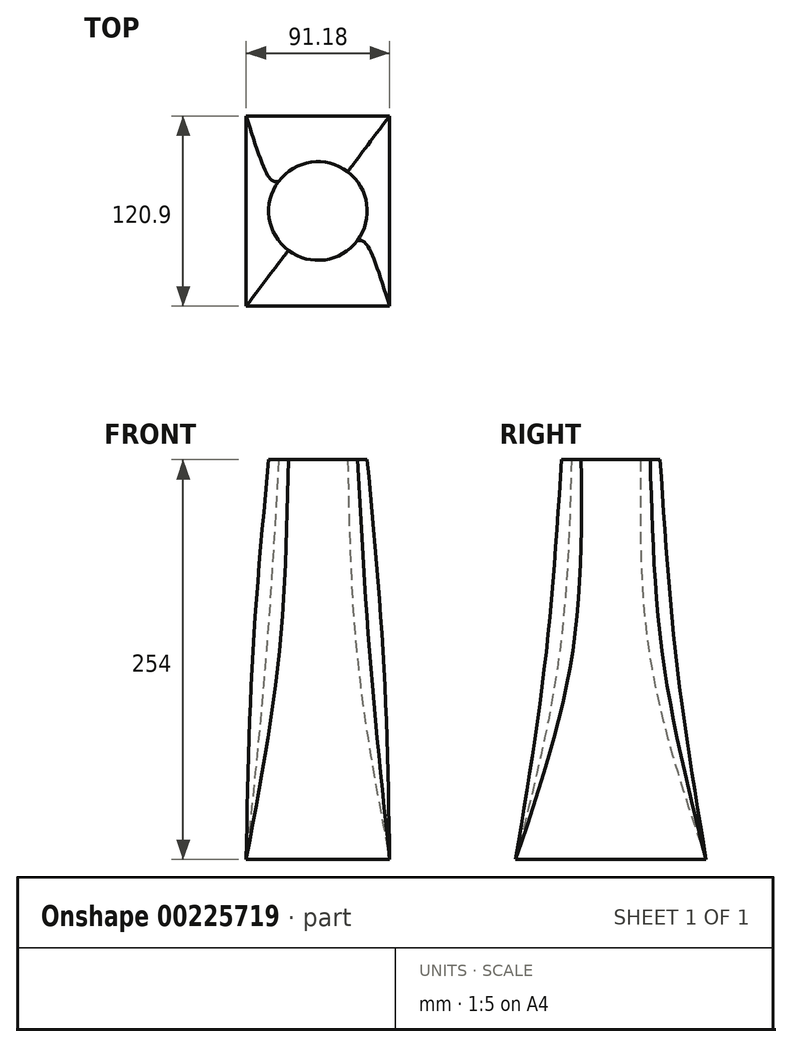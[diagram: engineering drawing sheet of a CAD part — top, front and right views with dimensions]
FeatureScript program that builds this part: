
annotation { "Feature Type Name" : "Feature", "Feature Type Description" : "" }
export const myFeature = defineFeature(function(context is Context, id is Id, definition is map)
    precondition{}
    {
        {
            var Q0;
            Q0=qCreatedBy(makeId("Top.planeOp"),FACE);
            var sketch = newSketch(context, id + "F0", { "sketchPlane" : qUnion([Q0])});
            skLineSegment(sketch, "E0.bottom", {"start": v(45.59, 60.45) * mm, "end": v(-45.59, 60.45) * mm});
            skLineSegment(sketch, "E0.top", {"start": v(45.59, -60.45) * mm, "end": v(-45.59, -60.45) * mm});
            skLineSegment(sketch, "E0.left", {"start": v(45.59, 60.45) * mm, "end": v(45.59, -60.45) * mm});
            skLineSegment(sketch, "E0.right", {"start": v(-45.59, 60.45) * mm, "end": v(-45.59, -60.45) * mm});
            skPoint(sketch, "E0.middle", {"position": v(0, 0) * mm});
            skSolve(sketch);
        }
        {
            var Q0;
            Q0=qCreatedBy(makeId("Top.planeOp"),FACE);
            cPlane(context, id + "F1", {"entities" : qUnion([Q0]), "cplaneType" : CPlaneType.OFFSET, "offset" : 254 * mm, "width" : 152.4 * mm, "height" : 152.4 * mm});
        }
        {
            var Q0;
            Q0=qCreatedBy(id+"F1.planeOp",FACE);
            var sketch = newSketch(context, id + "F2", { "sketchPlane" : qUnion([Q0])});
            skPoint(sketch, "E1.middle", {"position": v(0, 0) * mm});
            skCircle(sketch, "E2", {"center": v(0, 0) * mm, "radius": 31.3 * mm});
            skSolve(sketch);
        }
        {
            var Q0;
            Q0=qCreatedBy(id+"F1.planeOp",FACE);
            var Q1;
            Q1=qCreatedBy(makeId("Top.planeOp"),FACE);
            cPlane(context, id + "F3", {"entities" : qUnion([Q0, Q1]), "cplaneType" : CPlaneType.MID_PLANE, "offset" : 25.4 * mm, "width" : 152.4 * mm, "height" : 152.4 * mm});
        }
        {
            var Q0;
            Q0=qCreatedBy(id+"F3.planeOp",FACE);
            var sketch = newSketch(context, id + "F4", { "sketchPlane" : qUnion([Q0])});
            skCircle(sketch, "E3", {"center": v(0, 0) * mm, "radius": 41.6 * mm});
            skSolve(sketch);
        }
        {
            var Q0;
            Q0=makeQuery(id+"F2.imprint","IMPRINT",FACE,{"disambiguationData":[TD([[makeQuery(id+"F2.imprint","IMPRINT",EDGE,{"derivedFrom":sQuery(id+"F2.wireOp",EDGE,"E2")}),1.0]])]});
            var Q1;
            Q1=makeQuery(id+"F4.imprint","IMPRINT",FACE,{"disambiguationData":[TD([[makeQuery(id+"F4.imprint","IMPRINT",EDGE,{"derivedFrom":sQuery(id+"F4.wireOp",EDGE,"E3")}),1.0]])]});
            var Q2;
            Q2=makeQuery(id+"F0.imprint","IMPRINT",FACE,{"disambiguationData":[TD([[makeQuery(id+"F0.imprint","IMPRINT",EDGE,{"derivedFrom":sQuery(id+"F0.wireOp",EDGE,"E0.bottom")}),1.0]])]});
            loft(context, id + "F5", {"sheetProfilesArray" : [{ "sheetProfileEntities" : qUnion([Q0]) }, { "sheetProfileEntities" : qUnion([Q1]) }, { "sheetProfileEntities" : qUnion([Q2]) }]});
        }
    });
